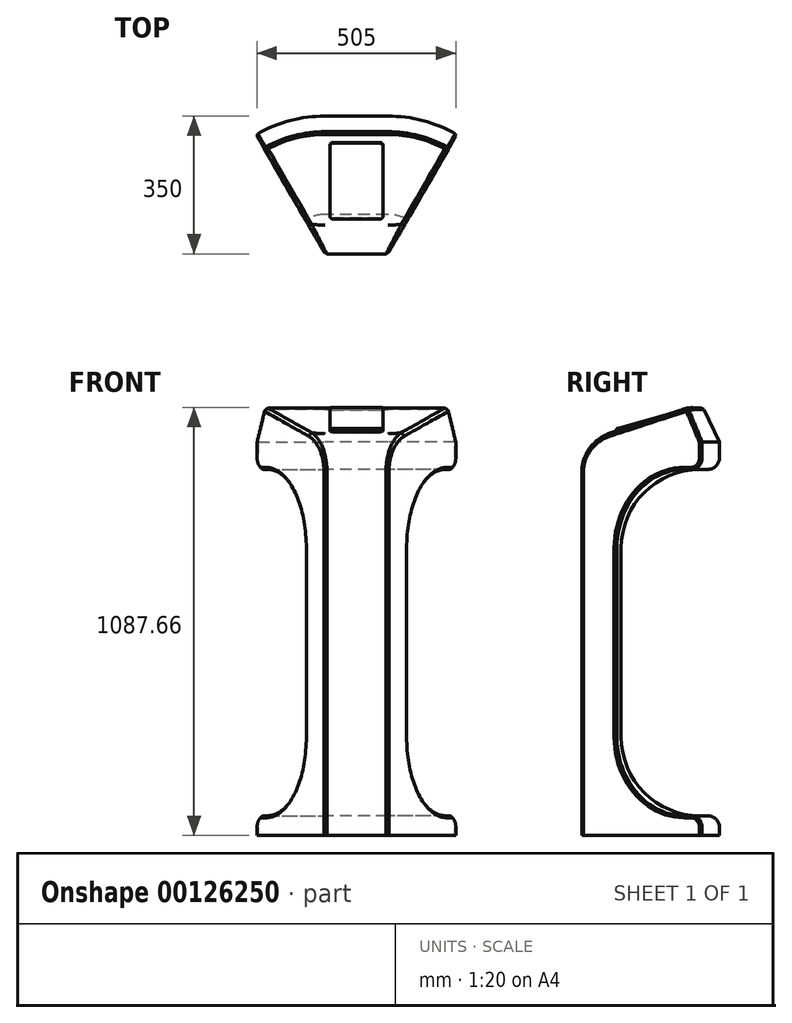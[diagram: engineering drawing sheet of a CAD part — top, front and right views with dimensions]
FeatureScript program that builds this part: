
annotation { "Feature Type Name" : "Feature", "Feature Type Description" : "" }
export const myFeature = defineFeature(function(context is Context, id is Id, definition is map)
    precondition{}
    {
        {
            var Q0;
            Q0=qCreatedBy(makeId("Right.planeOp"),FACE);
            var sketch = newSketch(context, id + "F0", { "sketchPlane" : qUnion([Q0])});
            skLineSegment(sketch, "E0.bottom", {"start": v(0, 0) * mm, "end": v(175, 0) * mm});
            skLineSegment(sketch, "E0.top", {"start": v(0, 1000) * mm, "end": v(175, 1000) * mm});
            skLineSegment(sketch, "E0.left", {"start": v(0, 0) * mm, "end": v(0, 93.88) * mm});
            skLineSegment(sketch, "E0.right", {"start": v(175, 0) * mm, "end": v(175, 20) * mm});
            skLineSegment(sketch, "E1.MirrorCS", {"start": v(-175, 0) * mm, "end": v(-175, 1000) * mm});
            skLineSegment(sketch, "E2.MirrorCS", {"start": v(0, 1000) * mm, "end": v(-175, 1000) * mm});
            skLineSegment(sketch, "E3.MirrorCS", {"start": v(0, 0) * mm, "end": v(-175, 0) * mm});
            skLineSegment(sketch, "E4", {"start": v(-175, 1000) * mm, "end": v(133.01, 1086.98) * mm});
            skLineSegment(sketch, "E5", {"start": v(133.01, 1086.98) * mm, "end": v(175, 1000) * mm});
            skLineSegment(sketch, "E6", {"start": v(175, 0) * mm, "end": v(175, 50) * mm, "construction": true});
            skLineSegment(sketch, "E7", {"start": v(175, 1000) * mm, "end": v(175, 930) * mm, "construction": true});
            skLineSegment(sketch, "E8.bottom", {"start": v(145, 930) * mm, "end": v(125, 930) * mm});
            skLineSegment(sketch, "E8.top", {"start": v(145, 50) * mm, "end": v(125, 50) * mm});
            skLineSegment(sketch, "E8.right", {"start": v(-75, 730) * mm, "end": v(-75, 250) * mm});
            skPoint(sketch, "E9.visualSharp", {"position": v(-75, 930) * mm});
            skArc(sketch, "E9.filletArc", {"start": v(125, 930) * mm, "mid": v(-16.42, 871.42) * mm, "end": v(-75, 730) * mm});
            skPoint(sketch, "E10.visualSharp", {"position": v(-75, 50) * mm});
            skArc(sketch, "E10.filletArc", {"start": v(-75, 250) * mm, "mid": v(-16.42, 108.58) * mm, "end": v(125, 50) * mm});
            skLineSegment(sketch, "E11.trimOffspring", {"start": v(175, 960) * mm, "end": v(175, 1000) * mm});
            skPoint(sketch, "E12.visualSharp", {"position": v(175, 930) * mm});
            skArc(sketch, "E12.filletArc", {"start": v(145, 930) * mm, "mid": v(166.21, 938.79) * mm, "end": v(175, 960) * mm});
            skPoint(sketch, "E13.visualSharp", {"position": v(175, 50) * mm});
            skArc(sketch, "E13.filletArc", {"start": v(175, 20) * mm, "mid": v(166.21, 41.21) * mm, "end": v(145, 50) * mm});
            skSolve(sketch);
        }
        {
            var Q0;
            Q0=makeQuery(id+"F0.imprint","IMPRINT",FACE,{"disambiguationData":[TD([[makeQuery(id+"F0.imprint","IMPRINT",EDGE,{"derivedFrom":sQuery(id+"F0.wireOp",EDGE,"E0.top")}),1.0]])]});
            var Q1;
            Q1=makeQuery(id+"F0.imprint","IMPRINT",FACE,{"disambiguationData":[TD([[makeQuery(id+"F0.imprint","IMPRINT",EDGE,{"derivedFrom":sQuery(id+"F0.wireOp",EDGE,"E0.left")}),1.0]])]});
            var Q2;
            Q2=makeQuery(id+"F0.imprint","IMPRINT",FACE,{"disambiguationData":[TD([[makeQuery(id+"F0.imprint","IMPRINT",EDGE,{"derivedFrom":sQuery(id+"F0.wireOp",EDGE,"E0.bottom")}),1.0]])]});
            extrude(context, id + "F1", {"entities" : qUnion([Q0, Q1, Q2]), "depth" : 160 * mm, "offsetDistance" : 25 * mm, "symmetric" : true});
        }
        {
            var Q0;
            Q0=makeQuery(id+"F1.opExtrude","CAP_FACE",FACE,{"disambiguationData":[OSD([sQuery(id+"F0.wireOp",EDGE,"E0.bottom"),sQuery(id+"F0.wireOp",EDGE,"E0.right"),sQuery(id+"F0.wireOp",EDGE,"E1.MirrorCS"),sQuery(id+"F0.wireOp",EDGE,"E3.MirrorCS"),sQuery(id+"F0.wireOp",EDGE,"E4"),sQuery(id+"F0.wireOp",EDGE,"E5")])],"isStart":false});
            var Q1;
            Q1=makeQuery(id+"F1.opExtrude","CAP_EDGE",EDGE,{"disambiguationData":[OSD([sQuery(id+"F0.wireOp",EDGE,"E1.MirrorCS")])],"isStart":false});
            revolve(context, id + "F2", {"operationType" : NewBodyOperationType.ADD, "surfaceOperationType" : NewSurfaceOperationType.NEW, "entities" : qUnion([Q0]), "axis" : qUnion([Q1]), "revolveType" : RevolveType.ONE_DIRECTION, "oppositeDirection" : true, "angle" : 30 * degree});
        }
        {
            var Q0;
            Q0=makeQuery(id+"F1.opExtrude","CAP_FACE",FACE,{"disambiguationData":[OSD([sQuery(id+"F0.wireOp",EDGE,"E0.bottom"),sQuery(id+"F0.wireOp",EDGE,"E0.right"),sQuery(id+"F0.wireOp",EDGE,"E1.MirrorCS"),sQuery(id+"F0.wireOp",EDGE,"E3.MirrorCS"),sQuery(id+"F0.wireOp",EDGE,"E4"),sQuery(id+"F0.wireOp",EDGE,"E5")])],"isStart":true});
            var Q1;
            Q1=makeQuery(id+"F1.opExtrude","CAP_EDGE",EDGE,{"disambiguationData":[OSD([sQuery(id+"F0.wireOp",EDGE,"E1.MirrorCS")])],"isStart":true});
            revolve(context, id + "F3", {"operationType" : NewBodyOperationType.ADD, "surfaceOperationType" : NewSurfaceOperationType.NEW, "entities" : qUnion([Q0]), "axis" : qUnion([Q1]), "revolveType" : RevolveType.ONE_DIRECTION, "angle" : 30 * degree});
        }
        {
            var Q0;
            Q0=makeQuery(id+"F1.opExtrude","SWEPT_EDGE",EDGE,{"disambiguationData":[OSD([sQuery(id+"F0.wireOp",EDGE,"E1.MirrorCS"),sQuery(id+"F0.wireOp",EDGE,"E2.MirrorCS"),sQuery(id+"F0.wireOp",EDGE,"E4")])]});
            fillet(context, id + "F4", {"entities" : qUnion([Q0]), "tangentPropagation" : true, "radius" : 100 * mm, "defaultsChanged" : true, "vertexSettings" : [], "allowEdgeOverflow" : false});
        }
        {
            var Q0;
            {var subQ0=sQuery(id+"F0.wireOp",EDGE,"E1.MirrorCS");Q0=makeQuery(id+"F2.boolean.opBoolean","MERGE",EDGE,{"derivedFrom":[makeQuery(id+"F1.opExtrude","CAP_EDGE",EDGE,{"disambiguationData":[OSD([subQ0])],"isStart":false}),makeQuery(id+"F2.opRevolve","CAP_EDGE",EDGE,{"disambiguationData":[OSD([subQ0])],"isStart":true})]});}
            var Q1;
            Q1=makeQuery(id+"F2.opRevolve","CAP_EDGE",EDGE,{"disambiguationData":[OSD([sQuery(id+"F0.wireOp",EDGE,"E4")])],"isStart":false});
            var Q2;
            Q2=makeQuery(id+"F2.opRevolve","CAP_EDGE",EDGE,{"disambiguationData":[OSD([sQuery(id+"F0.wireOp",EDGE,"E5")])],"isStart":false});
            var Q3;
            Q3=makeQuery(id+"F2.opRevolve","CAP_EDGE",EDGE,{"disambiguationData":[OSD([sQuery(id+"F0.wireOp",EDGE,"E12.filletArc")])],"isStart":false});
            var Q4;
            Q4=makeQuery(id+"F2.opRevolve","CAP_EDGE",EDGE,{"disambiguationData":[OSD([sQuery(id+"F0.wireOp",EDGE,"E11.trimOffspring")])],"isStart":false});
            var Q5;
            Q5=makeQuery(id+"F2.opRevolve","CAP_EDGE",EDGE,{"disambiguationData":[OSD([sQuery(id+"F0.wireOp",EDGE,"E8.bottom")])],"isStart":false});
            var Q6;
            Q6=makeQuery(id+"F2.opRevolve","CAP_EDGE",EDGE,{"disambiguationData":[OSD([sQuery(id+"F0.wireOp",EDGE,"E9.filletArc")])],"isStart":false});
            var Q7;
            Q7=makeQuery(id+"F2.opRevolve","CAP_EDGE",EDGE,{"disambiguationData":[OSD([sQuery(id+"F0.wireOp",EDGE,"E8.right")])],"isStart":false});
            var Q8;
            Q8=makeQuery(id+"F2.opRevolve","CAP_EDGE",EDGE,{"disambiguationData":[OSD([sQuery(id+"F0.wireOp",EDGE,"E10.filletArc")])],"isStart":false});
            var Q9;
            Q9=makeQuery(id+"F2.opRevolve","CAP_EDGE",EDGE,{"disambiguationData":[OSD([sQuery(id+"F0.wireOp",EDGE,"E13.filletArc")])],"isStart":false});
            var Q10;
            Q10=makeQuery(id+"F2.opRevolve","CAP_EDGE",EDGE,{"disambiguationData":[OSD([sQuery(id+"F0.wireOp",EDGE,"E8.top")])],"isStart":false});
            var Q11;
            Q11=makeQuery(id+"F2.opRevolve","CAP_EDGE",EDGE,{"disambiguationData":[OSD([sQuery(id+"F0.wireOp",EDGE,"E0.right")])],"isStart":false});
            var Q12;
            {var subQ0=sQuery(id+"F0.wireOp",EDGE,"E1.MirrorCS");Q12=makeQuery(id+"F3.boolean.opBoolean","MERGE",EDGE,{"derivedFrom":[makeQuery(id+"F1.opExtrude","CAP_EDGE",EDGE,{"disambiguationData":[OSD([subQ0])],"isStart":true}),makeQuery(id+"F3.opRevolve","CAP_EDGE",EDGE,{"disambiguationData":[OSD([subQ0])],"isStart":true})]});}
            var Q13;
            Q13=makeQuery(id+"F3.opRevolve","CAP_EDGE",EDGE,{"disambiguationData":[OSD([sQuery(id+"F0.wireOp",EDGE,"E4")])],"isStart":false});
            var Q14;
            Q14=makeQuery(id+"F3.opRevolve","CAP_EDGE",EDGE,{"disambiguationData":[OSD([sQuery(id+"F0.wireOp",EDGE,"E5")])],"isStart":false});
            var Q15;
            Q15=makeQuery(id+"F3.opRevolve","CAP_EDGE",EDGE,{"disambiguationData":[OSD([sQuery(id+"F0.wireOp",EDGE,"E11.trimOffspring")])],"isStart":false});
            var Q16;
            Q16=makeQuery(id+"F3.opRevolve","CAP_EDGE",EDGE,{"disambiguationData":[OSD([sQuery(id+"F0.wireOp",EDGE,"E8.bottom")])],"isStart":false});
            var Q17;
            Q17=makeQuery(id+"F3.opRevolve","CAP_EDGE",EDGE,{"disambiguationData":[OSD([sQuery(id+"F0.wireOp",EDGE,"E9.filletArc")])],"isStart":false});
            var Q18;
            Q18=makeQuery(id+"F3.opRevolve","CAP_EDGE",EDGE,{"disambiguationData":[OSD([sQuery(id+"F0.wireOp",EDGE,"E12.filletArc")])],"isStart":false});
            var Q19;
            Q19=makeQuery(id+"F3.opRevolve","CAP_EDGE",EDGE,{"disambiguationData":[OSD([sQuery(id+"F0.wireOp",EDGE,"E8.right")])],"isStart":false});
            var Q20;
            Q20=makeQuery(id+"F3.opRevolve","CAP_EDGE",EDGE,{"disambiguationData":[OSD([sQuery(id+"F0.wireOp",EDGE,"E10.filletArc")])],"isStart":false});
            var Q21;
            Q21=makeQuery(id+"F3.opRevolve","CAP_EDGE",EDGE,{"disambiguationData":[OSD([sQuery(id+"F0.wireOp",EDGE,"E0.right")])],"isStart":false});
            var Q22;
            Q22=makeQuery(id+"F3.opRevolve","CAP_EDGE",EDGE,{"disambiguationData":[OSD([sQuery(id+"F0.wireOp",EDGE,"E13.filletArc")])],"isStart":false});
            var Q23;
            Q23=makeQuery(id+"F3.opRevolve","CAP_EDGE",EDGE,{"disambiguationData":[OSD([sQuery(id+"F0.wireOp",EDGE,"E8.top")])],"isStart":false});
            var Q24;
            {var subQ0=sQuery(id+"F0.wireOp",EDGE,"E4");var subQ1=sQuery(id+"F0.wireOp",EDGE,"E1.MirrorCS");Q24=makeQuery(id+"F4.opFillet","BLEND_EDGE",EDGE,{"blendedFrom":[makeQuery(id+"F1.opExtrude","SWEPT_EDGE",EDGE,{"disambiguationData":[OSD([subQ1,sQuery(id+"F0.wireOp",EDGE,"E2.MirrorCS"),subQ0])]}),makeQuery(id+"F3.opRevolve","CAP_FACE",FACE,{"disambiguationData":[OSD([sQuery(id+"F0.wireOp",EDGE,"E0.bottom"),sQuery(id+"F0.wireOp",EDGE,"E0.right"),subQ1,sQuery(id+"F0.wireOp",EDGE,"E3.MirrorCS"),subQ0,sQuery(id+"F0.wireOp",EDGE,"E5"),sQuery(id+"F0.wireOp",EDGE,"E8.bottom"),sQuery(id+"F0.wireOp",EDGE,"E8.top"),sQuery(id+"F0.wireOp",EDGE,"E8.right"),sQuery(id+"F0.wireOp",EDGE,"E9.filletArc"),sQuery(id+"F0.wireOp",EDGE,"E10.filletArc"),sQuery(id+"F0.wireOp",EDGE,"E11.trimOffspring"),sQuery(id+"F0.wireOp",EDGE,"E12.filletArc"),sQuery(id+"F0.wireOp",EDGE,"E13.filletArc")])],"isStart":false})],"blendedInto":[makeQuery(id+"F3.opRevolve","CAP_FACE",FACE,{"disambiguationData":[OSD([sQuery(id+"F0.wireOp",EDGE,"E0.bottom"),sQuery(id+"F0.wireOp",EDGE,"E0.right"),subQ1,sQuery(id+"F0.wireOp",EDGE,"E3.MirrorCS"),subQ0,sQuery(id+"F0.wireOp",EDGE,"E5"),sQuery(id+"F0.wireOp",EDGE,"E8.bottom"),sQuery(id+"F0.wireOp",EDGE,"E8.top"),sQuery(id+"F0.wireOp",EDGE,"E8.right"),sQuery(id+"F0.wireOp",EDGE,"E9.filletArc"),sQuery(id+"F0.wireOp",EDGE,"E10.filletArc"),sQuery(id+"F0.wireOp",EDGE,"E11.trimOffspring"),sQuery(id+"F0.wireOp",EDGE,"E12.filletArc"),sQuery(id+"F0.wireOp",EDGE,"E13.filletArc")])],"isStart":false})]});}
            var Q25;
            {var subQ0=sQuery(id+"F0.wireOp",EDGE,"E4");var subQ1=sQuery(id+"F0.wireOp",EDGE,"E1.MirrorCS");Q25=makeQuery(id+"F4.opFillet","BLEND_EDGE",EDGE,{"blendedFrom":[makeQuery(id+"F1.opExtrude","SWEPT_EDGE",EDGE,{"disambiguationData":[OSD([subQ1,sQuery(id+"F0.wireOp",EDGE,"E2.MirrorCS"),subQ0])]}),makeQuery(id+"F2.opRevolve","CAP_FACE",FACE,{"disambiguationData":[OSD([sQuery(id+"F0.wireOp",EDGE,"E0.bottom"),sQuery(id+"F0.wireOp",EDGE,"E0.right"),subQ1,sQuery(id+"F0.wireOp",EDGE,"E3.MirrorCS"),subQ0,sQuery(id+"F0.wireOp",EDGE,"E5"),sQuery(id+"F0.wireOp",EDGE,"E8.bottom"),sQuery(id+"F0.wireOp",EDGE,"E8.top"),sQuery(id+"F0.wireOp",EDGE,"E8.right"),sQuery(id+"F0.wireOp",EDGE,"E9.filletArc"),sQuery(id+"F0.wireOp",EDGE,"E10.filletArc"),sQuery(id+"F0.wireOp",EDGE,"E11.trimOffspring"),sQuery(id+"F0.wireOp",EDGE,"E12.filletArc"),sQuery(id+"F0.wireOp",EDGE,"E13.filletArc")])],"isStart":false})],"blendedInto":[makeQuery(id+"F2.opRevolve","CAP_FACE",FACE,{"disambiguationData":[OSD([sQuery(id+"F0.wireOp",EDGE,"E0.bottom"),sQuery(id+"F0.wireOp",EDGE,"E0.right"),subQ1,sQuery(id+"F0.wireOp",EDGE,"E3.MirrorCS"),subQ0,sQuery(id+"F0.wireOp",EDGE,"E5"),sQuery(id+"F0.wireOp",EDGE,"E8.bottom"),sQuery(id+"F0.wireOp",EDGE,"E8.top"),sQuery(id+"F0.wireOp",EDGE,"E8.right"),sQuery(id+"F0.wireOp",EDGE,"E9.filletArc"),sQuery(id+"F0.wireOp",EDGE,"E10.filletArc"),sQuery(id+"F0.wireOp",EDGE,"E11.trimOffspring"),sQuery(id+"F0.wireOp",EDGE,"E12.filletArc"),sQuery(id+"F0.wireOp",EDGE,"E13.filletArc")])],"isStart":false})]});}
            var Q26;
            Q26=makeQuery(id+"F3.opRevolve","SWEPT_EDGE",EDGE,{"disambiguationData":[OSD([sQuery(id+"F0.wireOp",EDGE,"E4"),sQuery(id+"F0.wireOp",EDGE,"E5")])]});
            var Q27;
            Q27=makeQuery(id+"F2.opRevolve","SWEPT_EDGE",EDGE,{"disambiguationData":[OSD([sQuery(id+"F0.wireOp",EDGE,"E4"),sQuery(id+"F0.wireOp",EDGE,"E5")])]});
            var Q28;
            Q28=makeQuery(id+"F1.opExtrude","SWEPT_EDGE",EDGE,{"disambiguationData":[OSD([sQuery(id+"F0.wireOp",EDGE,"E4"),sQuery(id+"F0.wireOp",EDGE,"E5")])]});
            chamfer(context, id + "F5", {"entities" : qUnion([Q0, Q1, Q2, Q3, Q4, Q5, Q6, Q7, Q8, Q9, Q10, Q11, Q12, Q13, Q14, Q15, Q16, Q17, Q18, Q19, Q20, Q21, Q22, Q23, Q24, Q25, Q26, Q27, Q28]), "width" : 5 * mm});
        }
        {
            var Q0;
            Q0=makeQuery(id+"F1.opExtrude","SWEPT_FACE",FACE,{"disambiguationData":[OSD([sQuery(id+"F0.wireOp",EDGE,"E4")])]});
            var sketch = newSketch(context, id + "F6", { "sketchPlane" : qUnion([Q0])});
            skLineSegment(sketch, "E14.0.0", {"start": v(80, 179.01) * mm, "end": v(80, 416.13) * mm});
            skLineSegment(sketch, "E14.0.1", {"start": v(80, 416.13) * mm, "end": v(-80, 416.13) * mm});
            skLineSegment(sketch, "E14.0.2", {"start": v(-80, 416.13) * mm, "end": v(-80, 179.01) * mm});
            skLineSegment(sketch, "E14.0.3", {"start": v(-80, 179.01) * mm, "end": v(80, 179.01) * mm});
            skLineSegment(sketch, "E15", {"start": v(0, 416.13) * mm, "end": v(0, 179.01) * mm, "construction": true});
            skLineSegment(sketch, "E16", {"start": v(-80, 297.57) * mm, "end": v(80, 297.57) * mm, "construction": true});
            skLineSegment(sketch, "E17.bottom", {"start": v(59.5, 397.57) * mm, "end": v(-59.5, 397.57) * mm});
            skLineSegment(sketch, "E17.top", {"start": v(59.5, 197.57) * mm, "end": v(-59.5, 197.57) * mm});
            skLineSegment(sketch, "E17.left", {"start": v(67.5, 389.57) * mm, "end": v(67.5, 205.57) * mm});
            skLineSegment(sketch, "E17.right", {"start": v(-67.5, 389.57) * mm, "end": v(-67.5, 205.57) * mm});
            skPoint(sketch, "E17.middle", {"position": v(0, 297.57) * mm});
            skPoint(sketch, "E18.visualSharp", {"position": v(67.5, 397.57) * mm});
            skArc(sketch, "E18.filletArc", {"start": v(67.5, 389.57) * mm, "mid": v(65.16, 395.23) * mm, "end": v(59.5, 397.57) * mm});
            skPoint(sketch, "E19.visualSharp", {"position": v(67.5, 197.57) * mm});
            skArc(sketch, "E19.filletArc", {"start": v(59.5, 197.57) * mm, "mid": v(65.16, 199.91) * mm, "end": v(67.5, 205.57) * mm});
            skPoint(sketch, "E20.visualSharp", {"position": v(-67.5, 197.57) * mm});
            skArc(sketch, "E20.filletArc", {"start": v(-67.5, 205.57) * mm, "mid": v(-65.16, 199.91) * mm, "end": v(-59.5, 197.57) * mm});
            skPoint(sketch, "E21.visualSharp", {"position": v(-67.5, 397.57) * mm});
            skArc(sketch, "E21.filletArc", {"start": v(-59.5, 397.57) * mm, "mid": v(-65.16, 395.23) * mm, "end": v(-67.5, 389.57) * mm});
            skSolve(sketch);
        }
        {
            var Q0;
            Q0=makeQuery(id+"F6.imprint","IMPRINT",FACE,{"disambiguationData":[TD([[makeQuery(id+"F6.imprint","IMPRINT",EDGE,{"derivedFrom":sQuery(id+"F6.wireOp",EDGE,"E17.bottom")}),1.0]])]});
            extrude(context, id + "F7", {"entities" : qUnion([Q0]), "depth" : 8 * mm, "offsetDistance" : 25 * mm});
        }
    });
